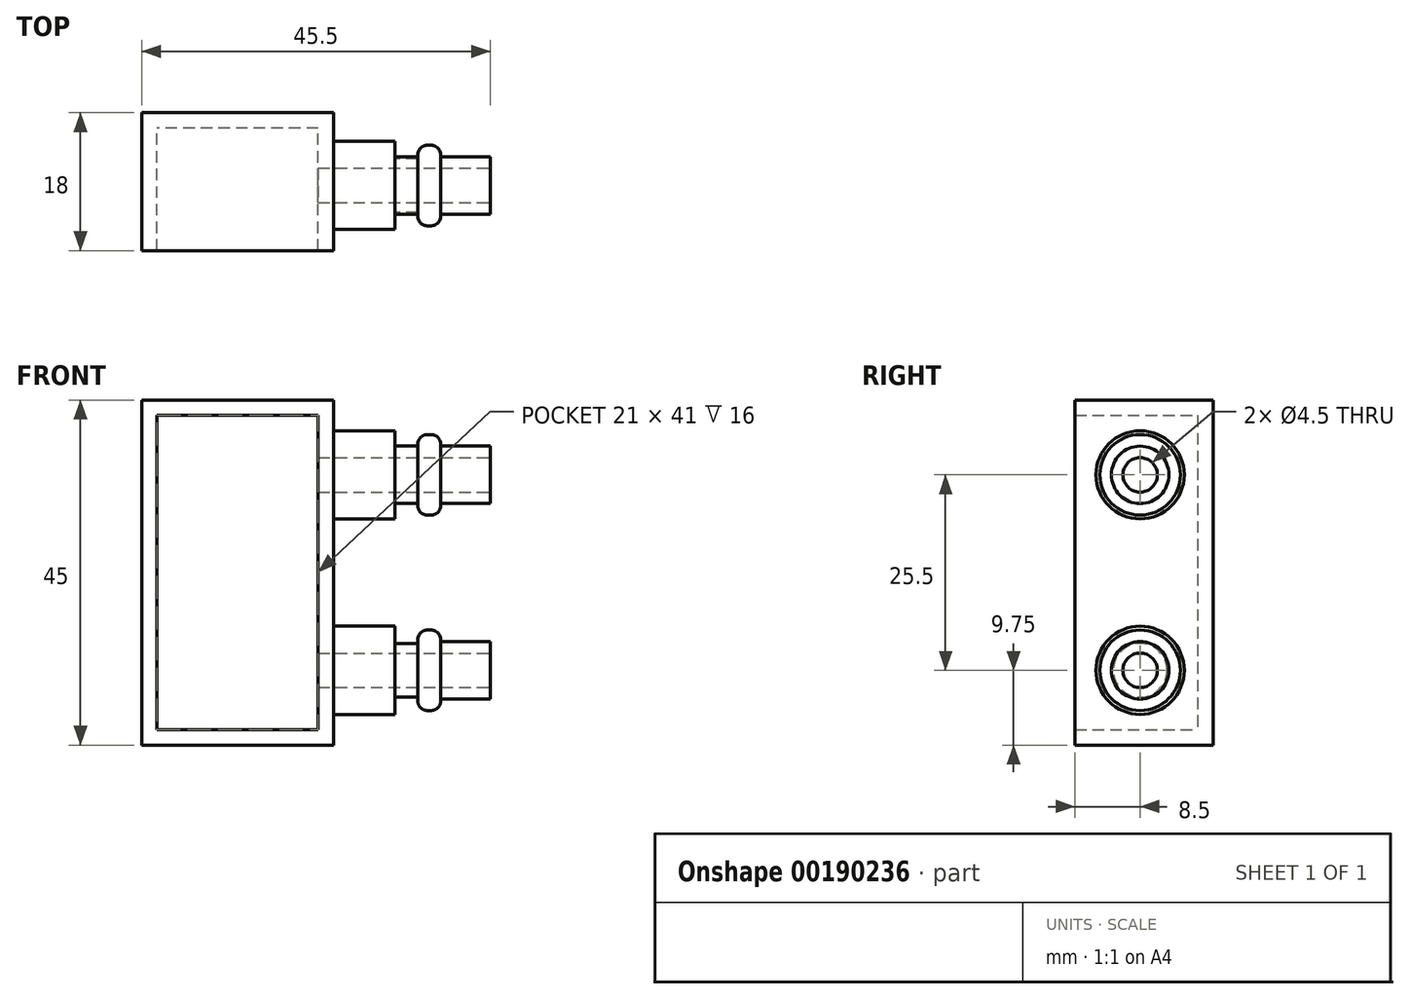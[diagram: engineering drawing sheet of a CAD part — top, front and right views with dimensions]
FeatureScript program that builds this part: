
annotation { "Feature Type Name" : "Feature", "Feature Type Description" : "" }
export const myFeature = defineFeature(function(context is Context, id is Id, definition is map)
    precondition{}
    {
        {
            var Q0;
            Q0=qCreatedBy(makeId("Front.planeOp"),FACE);
            var sketch = newSketch(context, id + "F0", { "sketchPlane" : qUnion([Q0])});
            skLineSegment(sketch, "E0.bottom", {"start": v(12.5, 22.5) * mm, "end": v(-12.5, 22.5) * mm});
            skLineSegment(sketch, "E0.top", {"start": v(12.5, -22.5) * mm, "end": v(-12.5, -22.5) * mm});
            skLineSegment(sketch, "E0.left", {"start": v(12.5, 22.5) * mm, "end": v(12.5, -22.5) * mm});
            skLineSegment(sketch, "E0.right", {"start": v(-12.5, 22.5) * mm, "end": v(-12.5, -22.5) * mm});
            skPoint(sketch, "E0.middle", {"position": v(0, 0) * mm});
            skSolve(sketch);
        }
        {
            var Q0;
            Q0 = qSketchRegion(id + "F0", true);
            extrude(context, id + "F1", {"entities" : qUnion([Q0]), "depth" : 2 * mm});
        }
        {
            var Q0;
            Q0=makeQuery(id+"F1.opExtrude","CAP_FACE",FACE,{"disambiguationData":[OSD([sQuery(id+"F0.wireOp",EDGE,"E0.bottom"),sQuery(id+"F0.wireOp",EDGE,"E0.top"),sQuery(id+"F0.wireOp",EDGE,"E0.left"),sQuery(id+"F0.wireOp",EDGE,"E0.right")])],"isStart":false});
            var sketch = newSketch(context, id + "F2", { "sketchPlane" : qUnion([Q0])});
            skLineSegment(sketch, "E1.bottom", {"start": v(12.5, 22.5) * mm, "end": v(-12.5, 22.5) * mm});
            skLineSegment(sketch, "E1.top", {"start": v(12.5, -22.5) * mm, "end": v(-12.5, -22.5) * mm});
            skLineSegment(sketch, "E1.left", {"start": v(12.5, 22.5) * mm, "end": v(12.5, -22.5) * mm});
            skLineSegment(sketch, "E1.right", {"start": v(-12.5, 22.5) * mm, "end": v(-12.5, -22.5) * mm});
            skPoint(sketch, "E1.middle", {"position": v(0, 0) * mm});
            skLineSegment(sketch, "E2.bottom", {"start": v(10.5, 20.5) * mm, "end": v(-10.5, 20.5) * mm});
            skLineSegment(sketch, "E2.top", {"start": v(10.5, -20.5) * mm, "end": v(-10.5, -20.5) * mm});
            skLineSegment(sketch, "E2.left", {"start": v(10.5, 20.5) * mm, "end": v(10.5, -20.5) * mm});
            skLineSegment(sketch, "E2.right", {"start": v(-10.5, 20.5) * mm, "end": v(-10.5, -20.5) * mm});
            skSolve(sketch);
        }
        {
            var Q0;
            Q0 = qSketchRegion(id + "F2", true);
            extrude(context, id + "F3", {"entities" : qUnion([Q0]), "operationType" : NewBodyOperationType.ADD, "depth" : 16 * mm});
        }
        {
            var Q0;
            Q0=makeQuery(id+"F3.boolean.opBoolean","MERGE",FACE,{"derivedFrom":[makeQuery(id+"F1.opExtrude","SWEPT_FACE",FACE,{"disambiguationData":[OSD([sQuery(id+"F0.wireOp",EDGE,"E0.left")])]}),makeQuery(id+"F3.opExtrude","SWEPT_FACE",FACE,{"disambiguationData":[OSD([sQuery(id+"F2.wireOp",EDGE,"E1.left")])]})]});
            var sketch = newSketch(context, id + "F4", { "sketchPlane" : qUnion([Q0])});
            skLineSegment(sketch, "E3.bottom", {"start": v(-18, 22.5) * mm, "end": v(-2, 22.5) * mm, "construction": true});
            skLineSegment(sketch, "E3.top", {"start": v(-18, -22.5) * mm, "end": v(-2, -22.5) * mm, "construction": true});
            skLineSegment(sketch, "E3.left", {"start": v(-18, 22.5) * mm, "end": v(-18, -22.5) * mm, "construction": true});
            skLineSegment(sketch, "E3.right", {"start": v(-2, 22.5) * mm, "end": v(-2, -22.5) * mm, "construction": true});
            skCircle(sketch, "E4", {"center": v(-9.5, 12.75) * mm, "radius": 5.75 * mm});
            skCircle(sketch, "E5", {"center": v(-9.5, -12.75) * mm, "radius": 5.75 * mm});
            skSolve(sketch);
        }
        {
            var Q0;
            Q0 = qSketchRegion(id + "F4", true);
            extrude(context, id + "F5", {"entities" : qUnion([Q0]), "operationType" : NewBodyOperationType.ADD, "depth" : 8 * mm});
        }
        {
            var Q0;
            Q0=makeQuery(id+"F5.opExtrude","CAP_FACE",FACE,{"disambiguationData":[OSD([sQuery(id+"F4.wireOp",EDGE,"E4")])],"isStart":false});
            var sketch = newSketch(context, id + "F6", { "sketchPlane" : qUnion([Q0])});
            skCircle(sketch, "E6", {"center": v(-9.5, 12.75) * mm, "radius": 3.75 * mm});
            skSolve(sketch);
        }
        {
            var Q0;
            Q0 = qSketchRegion(id + "F6", true);
            extrude(context, id + "F7", {"entities" : qUnion([Q0]), "operationType" : NewBodyOperationType.ADD, "depth" : 3 * mm});
        }
        {
            var Q0;
            Q0=makeQuery(id+"F5.opExtrude","CAP_FACE",FACE,{"disambiguationData":[OSD([sQuery(id+"F4.wireOp",EDGE,"E5")])],"isStart":false});
            var sketch = newSketch(context, id + "F8", { "sketchPlane" : qUnion([Q0])});
            skCircle(sketch, "E7", {"center": v(-9.5, -12.75) * mm, "radius": 3.5 * mm});
            skSolve(sketch);
        }
        {
            var Q0;
            Q0 = qSketchRegion(id + "F8", true);
            extrude(context, id + "F9", {"entities" : qUnion([Q0]), "operationType" : NewBodyOperationType.ADD, "depth" : 3 * mm});
        }
        {
            var Q0;
            Q0=makeQuery(id+"F7.opExtrude","CAP_FACE",FACE,{"disambiguationData":[OSD([sQuery(id+"F6.wireOp",EDGE,"E6")])],"isStart":false});
            var sketch = newSketch(context, id + "F10", { "sketchPlane" : qUnion([Q0])});
            skCircle(sketch, "E8", {"center": v(-9.5, 12.75) * mm, "radius": 5.25 * mm});
            skSolve(sketch);
        }
        {
            var Q0;
            Q0 = qSketchRegion(id + "F10", true);
            extrude(context, id + "F11", {"entities" : qUnion([Q0]), "operationType" : NewBodyOperationType.ADD, "depth" : 3 * mm});
        }
        {
            var Q0;
            Q0=makeQuery(id+"F9.opExtrude","CAP_FACE",FACE,{"disambiguationData":[OSD([sQuery(id+"F8.wireOp",EDGE,"E7")])],"isStart":false});
            var sketch = newSketch(context, id + "F12", { "sketchPlane" : qUnion([Q0])});
            skCircle(sketch, "E9", {"center": v(-9.5, -12.75) * mm, "radius": 5.25 * mm});
            skSolve(sketch);
        }
        {
            var Q0;
            Q0 = qSketchRegion(id + "F12", true);
            extrude(context, id + "F13", {"entities" : qUnion([Q0]), "operationType" : NewBodyOperationType.ADD, "depth" : 3 * mm});
        }
        {
            var Q0;
            Q0=makeQuery(id+"F11.opExtrude","CAP_FACE",FACE,{"disambiguationData":[OSD([sQuery(id+"F10.wireOp",EDGE,"E8")])],"isStart":false});
            var sketch = newSketch(context, id + "F14", { "sketchPlane" : qUnion([Q0])});
            skCircle(sketch, "E10", {"center": v(-9.5, 12.75) * mm, "radius": 3.75 * mm});
            skSolve(sketch);
        }
        {
            var Q0;
            Q0 = qSketchRegion(id + "F14", true);
            extrude(context, id + "F15", {"entities" : qUnion([Q0]), "operationType" : NewBodyOperationType.ADD, "depth" : 6.5 * mm});
        }
        {
            var Q0;
            Q0=makeQuery(id+"F13.opExtrude","CAP_FACE",FACE,{"disambiguationData":[OSD([sQuery(id+"F12.wireOp",EDGE,"E9")])],"isStart":false});
            var sketch = newSketch(context, id + "F16", { "sketchPlane" : qUnion([Q0])});
            skCircle(sketch, "E11", {"center": v(-9.5, -12.75) * mm, "radius": 3.75 * mm});
            skSolve(sketch);
        }
        {
            var Q0;
            Q0 = qSketchRegion(id + "F16", true);
            extrude(context, id + "F17", {"entities" : qUnion([Q0]), "operationType" : NewBodyOperationType.ADD, "depth" : 6.5 * mm});
        }
        {
            var Q0;
            Q0=makeQuery(id+"F11.opExtrude","CAP_EDGE",EDGE,{"disambiguationData":[OSD([sQuery(id+"F10.wireOp",EDGE,"E8")])],"isStart":false});
            var Q1;
            Q1=makeQuery(id+"F13.opExtrude","CAP_EDGE",EDGE,{"disambiguationData":[OSD([sQuery(id+"F12.wireOp",EDGE,"E9")])],"isStart":false});
            var Q2;
            Q2=makeQuery(id+"F13.opExtrude","CAP_EDGE",EDGE,{"disambiguationData":[OSD([sQuery(id+"F12.wireOp",EDGE,"E9")])],"isStart":true});
            var Q3;
            Q3=makeQuery(id+"F11.opExtrude","CAP_EDGE",EDGE,{"disambiguationData":[OSD([sQuery(id+"F10.wireOp",EDGE,"E8")])],"isStart":true});
            fillet(context, id + "F18", {"entities" : qUnion([Q0, Q1, Q2, Q3]), "radius" : 1.25 * mm, "tangentPropagation" : true, "allowEdgeOverflow" : false});
        }
        {
            var Q0;
            Q0=makeQuery(id+"F15.opExtrude","CAP_FACE",FACE,{"disambiguationData":[OSD([sQuery(id+"F14.wireOp",EDGE,"E10")])],"isStart":false});
            var sketch = newSketch(context, id + "F19", { "sketchPlane" : qUnion([Q0])});
            skCircle(sketch, "E12", {"center": v(-9.5, 12.75) * mm, "radius": 2.25 * mm});
            skSolve(sketch);
        }
        {
            var Q0;
            Q0 = qSketchRegion(id + "F19", true);
            extrude(context, id + "F20", {"entities" : qUnion([Q0]), "operationType" : NewBodyOperationType.REMOVE, "oppositeDirection" : true, "depth" : 25 * mm});
        }
        {
            var Q0;
            Q0=makeQuery(id+"F17.opExtrude","CAP_FACE",FACE,{"disambiguationData":[OSD([sQuery(id+"F16.wireOp",EDGE,"E11")])],"isStart":false});
            var sketch = newSketch(context, id + "F21", { "sketchPlane" : qUnion([Q0])});
            skCircle(sketch, "E13", {"center": v(-9.5, -12.75) * mm, "radius": 2.25 * mm});
            skSolve(sketch);
        }
        {
            var Q0;
            Q0 = qSketchRegion(id + "F21", true);
            extrude(context, id + "F22", {"entities" : qUnion([Q0]), "operationType" : NewBodyOperationType.REMOVE, "oppositeDirection" : true, "depth" : 25 * mm});
        }
    });
